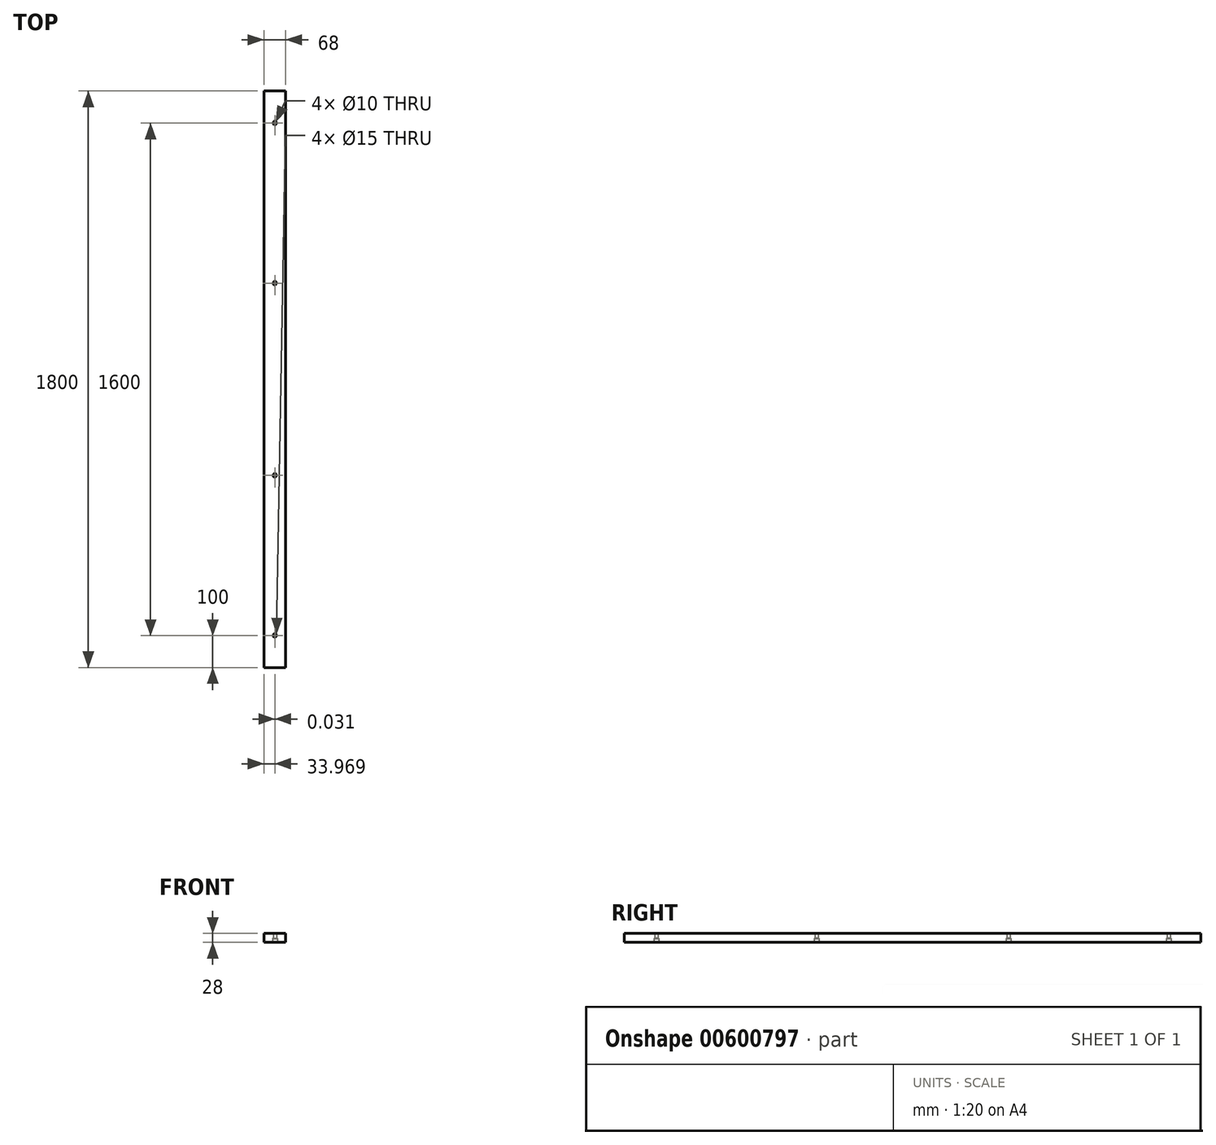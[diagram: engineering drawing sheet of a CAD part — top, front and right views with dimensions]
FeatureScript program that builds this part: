
annotation { "Feature Type Name" : "Feature", "Feature Type Description" : "" }
export const myFeature = defineFeature(function(context is Context, id is Id, definition is map)
    precondition{}
    {
        {
            var Q0;
            Q0=qCreatedBy(makeId("Front.planeOp"),FACE);
            var sketch = newSketch(context, id + "F0", { "sketchPlane" : qUnion([Q0])});
            skLineSegment(sketch, "E0.bottom", {"start": v(0, 0) * mm, "end": v(-68, 0) * mm});
            skLineSegment(sketch, "E0.top", {"start": v(0, 28) * mm, "end": v(-68, 28) * mm});
            skLineSegment(sketch, "E0.left", {"start": v(0, 0) * mm, "end": v(0, 28) * mm});
            skLineSegment(sketch, "E0.right", {"start": v(-68, 0) * mm, "end": v(-68, 28) * mm});
            skSolve(sketch);
        }
        {
            var Q0;
            Q0=makeQuery(id+"F0.imprint","IMPRINT",FACE,{"disambiguationData":[TD([[makeQuery(id+"F0.imprint","IMPRINT",EDGE,{"derivedFrom":sQuery(id+"F0.wireOp",EDGE,"E0.bottom")}),-1.0]])]});
            extrude(context, id + "F1", {"entities" : qUnion([Q0]), "endBound" : BoundingType.SYMMETRIC, "depth" : 1800 * mm, "offsetDistance" : 25 * mm});
        }
        {
            var Q0;
            Q0=qCreatedBy(makeId("Top.planeOp"),FACE);
            var sketch = newSketch(context, id + "F2", { "sketchPlane" : qUnion([Q0])});
            skLineSegment(sketch, "E1", {"start": v(0, -800) * mm, "end": v(-34, -800) * mm});
            skCircle(sketch, "E2", {"center": v(-34.02, -300) * mm, "radius": 7.5 * mm});
            skCircle(sketch, "E3", {"center": v(-34, 300) * mm, "radius": 7.5 * mm});
            skCircle(sketch, "E4", {"center": v(-34.02, -300) * mm, "radius": 5 * mm});
            skCircle(sketch, "E5", {"center": v(-34, 300) * mm, "radius": 5 * mm});
            skLineSegment(sketch, "E6", {"start": v(0, 800) * mm, "end": v(-68.06, 800) * mm, "construction": true});
            skCircle(sketch, "E7", {"center": v(-34.03, 800) * mm, "radius": 7.5 * mm});
            skCircle(sketch, "E8", {"center": v(-34.03, 800) * mm, "radius": 5 * mm});
            skSolve(sketch);
        }
        {
            var Q0;
            Q0=sQuery(id+"F2.wireOp",VERTEX,"E2.center");
            var Q1;
            Q1=makeQuery(id+"F1.opExtrude","SWEPT_BODY",BODY,{"disambiguationData":[OSD([sQuery(id+"F0.wireOp",EDGE,"E0.bottom"),sQuery(id+"F0.wireOp",EDGE,"E0.top"),sQuery(id+"F0.wireOp",EDGE,"E0.left"),sQuery(id+"F0.wireOp",EDGE,"E0.right")])]});
            hole(context, id + "F3", {"style" : HoleStyle.SIMPLE, "endStyle" : HoleEndStyle.THROUGH, "oppositeDirection" : true, "holeDiameter" : 10 * mm, "majorDiameter" : 5 * mm, "isTappedThrough" : true, "tappedDepth" : 12 * mm, "tapClearance" : 3, "locations" : qUnion([Q0]), "scope" : qUnion([Q1])});
        }
        {
            var Q0;
            Q0=sQuery(id+"F2.wireOp",VERTEX,"E2.center");
            var Q1;
            Q1=makeQuery(id+"F1.opExtrude","SWEPT_BODY",BODY,{"disambiguationData":[OSD([sQuery(id+"F0.wireOp",EDGE,"E0.bottom"),sQuery(id+"F0.wireOp",EDGE,"E0.top"),sQuery(id+"F0.wireOp",EDGE,"E0.left"),sQuery(id+"F0.wireOp",EDGE,"E0.right")])]});
            hole(context, id + "F4", {"style" : HoleStyle.SIMPLE, "endStyle" : HoleEndStyle.BLIND, "oppositeDirection" : true, "holeDiameter" : 15 * mm, "majorDiameter" : 5 * mm, "holeDepth" : 12 * mm, "isTappedThrough" : true, "tappedDepth" : 12 * mm, "tapClearance" : 3, "locations" : qUnion([Q0]), "scope" : qUnion([Q1])});
        }
        {
            var Q0;
            Q0=sQuery(id+"F2.wireOp",VERTEX,"E3.center");
            var Q1;
            Q1=makeQuery(id+"F1.opExtrude","SWEPT_BODY",BODY,{"disambiguationData":[OSD([sQuery(id+"F0.wireOp",EDGE,"E0.bottom"),sQuery(id+"F0.wireOp",EDGE,"E0.top"),sQuery(id+"F0.wireOp",EDGE,"E0.left"),sQuery(id+"F0.wireOp",EDGE,"E0.right")])]});
            hole(context, id + "F5", {"style" : HoleStyle.SIMPLE, "endStyle" : HoleEndStyle.THROUGH, "oppositeDirection" : true, "holeDiameter" : 10 * mm, "majorDiameter" : 5 * mm, "isTappedThrough" : true, "tappedDepth" : 12 * mm, "tapClearance" : 3, "locations" : qUnion([Q0]), "scope" : qUnion([Q1])});
        }
        {
            var Q0;
            Q0=sQuery(id+"F2.wireOp",VERTEX,"E3.center");
            var Q1;
            Q1=makeQuery(id+"F1.opExtrude","SWEPT_BODY",BODY,{"disambiguationData":[OSD([sQuery(id+"F0.wireOp",EDGE,"E0.bottom"),sQuery(id+"F0.wireOp",EDGE,"E0.top"),sQuery(id+"F0.wireOp",EDGE,"E0.left"),sQuery(id+"F0.wireOp",EDGE,"E0.right")])]});
            hole(context, id + "F6", {"style" : HoleStyle.SIMPLE, "endStyle" : HoleEndStyle.BLIND, "oppositeDirection" : true, "holeDiameter" : 15 * mm, "majorDiameter" : 5 * mm, "holeDepth" : 12 * mm, "isTappedThrough" : true, "tappedDepth" : 12 * mm, "tapClearance" : 3, "locations" : qUnion([Q0]), "scope" : qUnion([Q1])});
        }
        {
            var Q0;
            Q0=sQuery(id+"F2.wireOp",VERTEX,"E1.end");
            var Q1;
            Q1=makeQuery(id+"F1.opExtrude","SWEPT_BODY",BODY,{"disambiguationData":[OSD([sQuery(id+"F0.wireOp",EDGE,"E0.bottom"),sQuery(id+"F0.wireOp",EDGE,"E0.top"),sQuery(id+"F0.wireOp",EDGE,"E0.left"),sQuery(id+"F0.wireOp",EDGE,"E0.right")])]});
            hole(context, id + "F7", {"style" : HoleStyle.SIMPLE, "endStyle" : HoleEndStyle.BLIND, "oppositeDirection" : true, "holeDiameter" : 15 * mm, "majorDiameter" : 5 * mm, "holeDepth" : 12 * mm, "isTappedThrough" : true, "tappedDepth" : 12 * mm, "tapClearance" : 3, "locations" : qUnion([Q0]), "scope" : qUnion([Q1])});
        }
        {
            var Q0;
            Q0=sQuery(id+"F2.wireOp",VERTEX,"E1.end");
            var Q1;
            Q1=makeQuery(id+"F1.opExtrude","SWEPT_BODY",BODY,{"disambiguationData":[OSD([sQuery(id+"F0.wireOp",EDGE,"E0.bottom"),sQuery(id+"F0.wireOp",EDGE,"E0.top"),sQuery(id+"F0.wireOp",EDGE,"E0.left"),sQuery(id+"F0.wireOp",EDGE,"E0.right")])]});
            hole(context, id + "F8", {"style" : HoleStyle.SIMPLE, "endStyle" : HoleEndStyle.THROUGH, "oppositeDirection" : true, "holeDiameter" : 10 * mm, "majorDiameter" : 5 * mm, "isTappedThrough" : true, "tappedDepth" : 12 * mm, "tapClearance" : 3, "locations" : qUnion([Q0]), "scope" : qUnion([Q1])});
        }
        {
            var Q0;
            Q0=sQuery(id+"F2.wireOp",VERTEX,"E8.center");
            var Q1;
            Q1=makeQuery(id+"F1.opExtrude","SWEPT_BODY",BODY,{"disambiguationData":[OSD([sQuery(id+"F0.wireOp",EDGE,"E0.bottom"),sQuery(id+"F0.wireOp",EDGE,"E0.top"),sQuery(id+"F0.wireOp",EDGE,"E0.left"),sQuery(id+"F0.wireOp",EDGE,"E0.right")])]});
            hole(context, id + "F9", {"style" : HoleStyle.SIMPLE, "endStyle" : HoleEndStyle.THROUGH, "oppositeDirection" : true, "holeDiameter" : 10 * mm, "majorDiameter" : 5 * mm, "isTappedThrough" : true, "tappedDepth" : 12 * mm, "tapClearance" : 3, "locations" : qUnion([Q0]), "scope" : qUnion([Q1])});
        }
        {
            var Q0;
            Q0=sQuery(id+"F2.wireOp",VERTEX,"E8.center");
            var Q1;
            Q1=makeQuery(id+"F1.opExtrude","SWEPT_BODY",BODY,{"disambiguationData":[OSD([sQuery(id+"F0.wireOp",EDGE,"E0.bottom"),sQuery(id+"F0.wireOp",EDGE,"E0.top"),sQuery(id+"F0.wireOp",EDGE,"E0.left"),sQuery(id+"F0.wireOp",EDGE,"E0.right")])]});
            hole(context, id + "F10", {"style" : HoleStyle.SIMPLE, "endStyle" : HoleEndStyle.BLIND, "oppositeDirection" : true, "holeDiameter" : 15 * mm, "majorDiameter" : 5 * mm, "holeDepth" : 12 * mm, "isTappedThrough" : true, "tappedDepth" : 12 * mm, "tapClearance" : 3, "locations" : qUnion([Q0]), "scope" : qUnion([Q1])});
        }
    });
